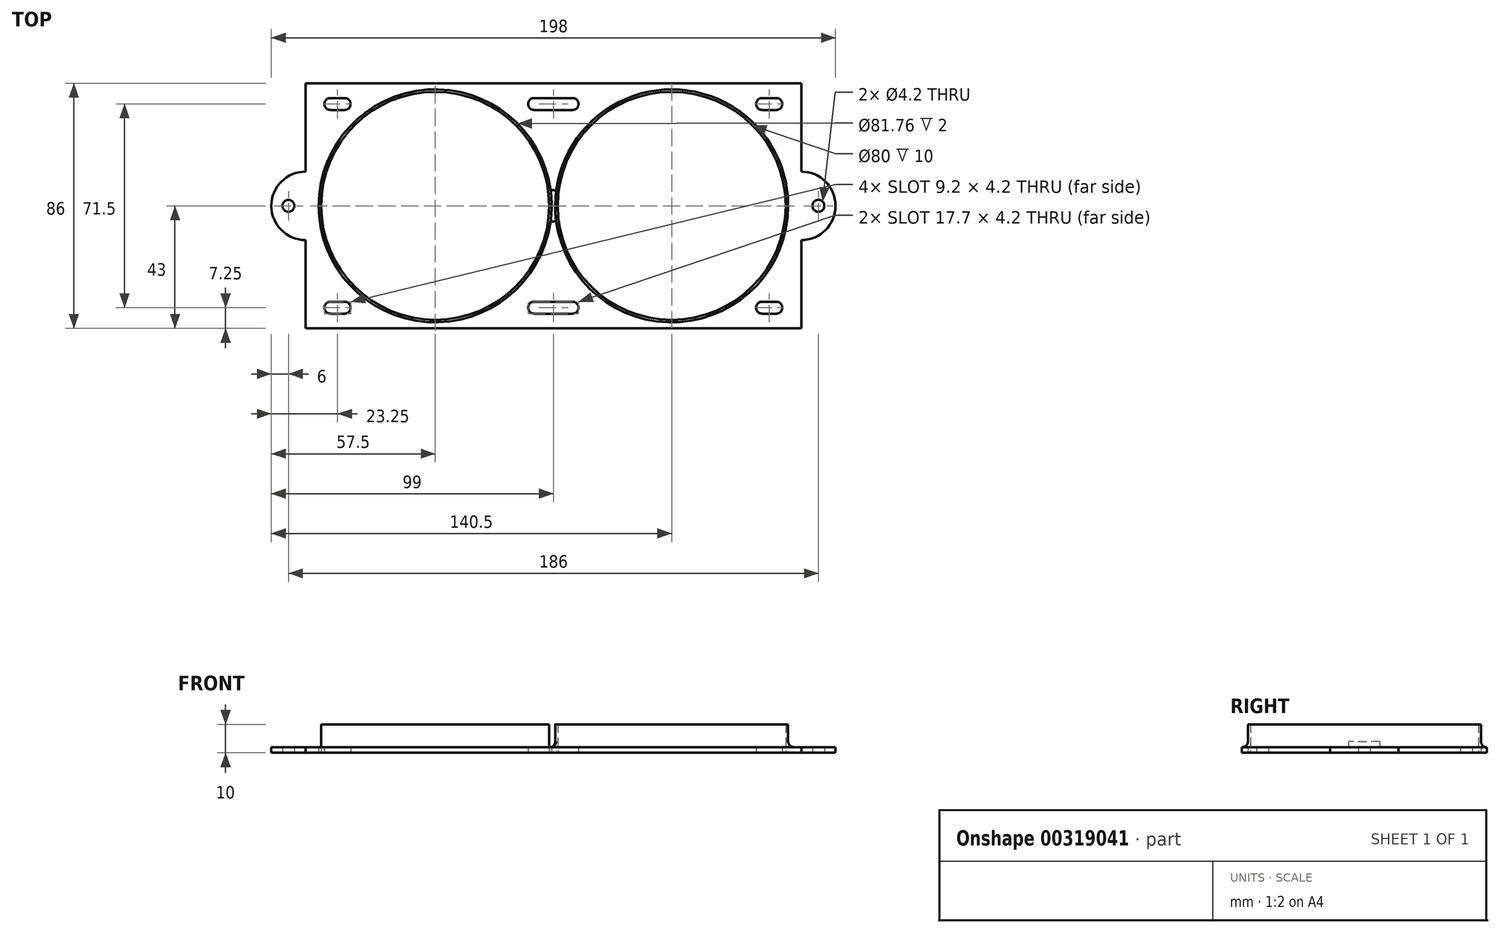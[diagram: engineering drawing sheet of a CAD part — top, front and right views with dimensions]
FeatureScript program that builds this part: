
annotation { "Feature Type Name" : "Feature", "Feature Type Description" : "" }
export const myFeature = defineFeature(function(context is Context, id is Id, definition is map)
    precondition{}
    {
        {
            var Q0;
            Q0=qCreatedBy(makeId("Top.planeOp"),FACE);
            var sketch = newSketch(context, id + "F0", { "sketchPlane" : qUnion([Q0])});
            skCircle(sketch, "E0", {"center": v(0, 0) * mm, "radius": 40 * mm});
            skLineSegment(sketch, "E1.bottom", {"start": v(35.75, -35.75) * mm, "end": v(-35.75, -35.75) * mm, "construction": true});
            skLineSegment(sketch, "E1.top", {"start": v(35.75, 35.75) * mm, "end": v(-35.75, 35.75) * mm, "construction": true});
            skLineSegment(sketch, "E1.left", {"start": v(35.75, -35.75) * mm, "end": v(35.75, 35.75) * mm, "construction": true});
            skLineSegment(sketch, "E1.right", {"start": v(-35.75, -35.75) * mm, "end": v(-35.75, 35.75) * mm, "construction": true});
            skLineSegment(sketch, "E2.bottom", {"start": v(41.5, -43) * mm, "end": v(-41.5, -43) * mm});
            skLineSegment(sketch, "E2.top", {"start": v(41.5, 43) * mm, "end": v(-41.5, 43) * mm});
            skLineSegment(sketch, "E2.left", {"start": v(41.5, -43) * mm, "end": v(41.5, 43) * mm});
            skLineSegment(sketch, "E2.right", {"start": v(-41.5, -43) * mm, "end": v(-41.5, 43) * mm});
            skLineSegment(sketch, "E3.bottom", {"start": v(45.5, 43) * mm, "end": v(41.5, 43) * mm});
            skLineSegment(sketch, "E3.top", {"start": v(45.5, -43) * mm, "end": v(41.5, -43) * mm});
            skLineSegment(sketch, "E3.left", {"start": v(45.5, 43) * mm, "end": v(45.5, -43) * mm});
            skLineSegment(sketch, "E3.right", {"start": v(41.5, 43) * mm, "end": v(41.5, -43) * mm});
            skLineSegment(sketch, "E4", {"start": v(36.75, 35.75) * mm, "end": v(31.75, 35.75) * mm});
            skArc(sketch, "E5.0.startCap", {"start": v(36.75, 37.85) * mm, "mid": v(38.85, 35.75) * mm, "end": v(36.75, 33.65) * mm});
            skArc(sketch, "E5.0.endCap", {"start": v(31.75, 33.65) * mm, "mid": v(29.65, 35.75) * mm, "end": v(31.75, 37.85) * mm});
            skLineSegment(sketch, "E5.0.left", {"start": v(36.75, 33.65) * mm, "end": v(31.75, 33.65) * mm});
            skLineSegment(sketch, "E5.0.right", {"start": v(36.75, 37.85) * mm, "end": v(31.75, 37.85) * mm});
            skArc(sketch, "E6.MirrorCS", {"start": v(-119.75, 37.85) * mm, "mid": v(-121.85, 35.75) * mm, "end": v(-119.75, 33.65) * mm});
            skArc(sketch, "E7.MirrorCS", {"start": v(-114.75, 33.65) * mm, "mid": v(-112.65, 35.75) * mm, "end": v(-114.75, 37.85) * mm});
            skLineSegment(sketch, "E8.MirrorCS", {"start": v(-119.75, 37.85) * mm, "end": v(-114.75, 37.85) * mm});
            skLineSegment(sketch, "E9.MirrorCS", {"start": v(-119.75, 33.65) * mm, "end": v(-114.75, 33.65) * mm});
            skLineSegment(sketch, "E10.MirrorCS", {"start": v(-119.75, 35.75) * mm, "end": v(-114.75, 35.75) * mm});
            skLineSegment(sketch, "E11.MirrorCS", {"start": v(-124.5, -43) * mm, "end": v(-124.5, 43) * mm});
            skPoint(sketch, "E12.MirrorP", {"position": v(-83, 0) * mm});
            skLineSegment(sketch, "E13.MirrorCS", {"start": v(-118.75, -35.75) * mm, "end": v(-47.25, -35.75) * mm, "construction": true});
            skLineSegment(sketch, "E14.MirrorCS", {"start": v(-124.5, 43) * mm, "end": v(-124.5, -43) * mm});
            skLineSegment(sketch, "E15.MirrorCS", {"start": v(-124.5, 43) * mm, "end": v(-41.5, 43) * mm});
            skLineSegment(sketch, "E16.MirrorCS", {"start": v(-47.25, -35.75) * mm, "end": v(-47.25, 35.75) * mm, "construction": true});
            skLineSegment(sketch, "E17.MirrorCS", {"start": v(-118.75, 35.75) * mm, "end": v(-47.25, 35.75) * mm, "construction": true});
            skCircle(sketch, "E18.MirrorC", {"center": v(-83, 0) * mm, "radius": 40 * mm});
            skLineSegment(sketch, "E19.MirrorCS", {"start": v(-124.5, -43) * mm, "end": v(-41.5, -43) * mm});
            skLineSegment(sketch, "E20.MirrorCS", {"start": v(-118.75, -35.75) * mm, "end": v(-118.75, 35.75) * mm, "construction": true});
            skLineSegment(sketch, "E21", {"start": v(0, 0) * mm, "end": v(-83, 0) * mm, "construction": true});
            skLineSegment(sketch, "E22", {"start": v(-40, 0) * mm, "end": v(-43, 0) * mm, "construction": true});
            skLineSegment(sketch, "E23", {"start": v(-34.75, 35.75) * mm, "end": v(-48.25, 35.75) * mm, "construction": true});
            skArc(sketch, "E24.0.startCap", {"start": v(-34.75, 37.85) * mm, "mid": v(-32.65, 35.75) * mm, "end": v(-34.75, 33.65) * mm});
            skArc(sketch, "E24.0.endCap", {"start": v(-48.25, 33.65) * mm, "mid": v(-50.35, 35.75) * mm, "end": v(-48.25, 37.85) * mm});
            skLineSegment(sketch, "E24.0.left", {"start": v(-34.75, 33.65) * mm, "end": v(-48.25, 33.65) * mm});
            skLineSegment(sketch, "E24.0.right", {"start": v(-34.75, 37.85) * mm, "end": v(-48.25, 37.85) * mm});
            skArc(sketch, "E25.MirrorCS", {"start": v(-48.25, -33.65) * mm, "mid": v(-50.35, -35.75) * mm, "end": v(-48.25, -37.85) * mm});
            skLineSegment(sketch, "E26.MirrorCS", {"start": v(-34.75, -33.65) * mm, "end": v(-48.25, -33.65) * mm});
            skArc(sketch, "E27.MirrorCS", {"start": v(-34.75, -37.85) * mm, "mid": v(-32.65, -35.75) * mm, "end": v(-34.75, -33.65) * mm});
            skLineSegment(sketch, "E28.MirrorCS", {"start": v(-34.75, -35.75) * mm, "end": v(-48.25, -35.75) * mm, "construction": true});
            skLineSegment(sketch, "E29.MirrorCS", {"start": v(-34.75, -37.85) * mm, "end": v(-48.25, -37.85) * mm});
            skLineSegment(sketch, "E30.MirrorCS", {"start": v(36.75, -37.85) * mm, "end": v(31.75, -37.85) * mm});
            skLineSegment(sketch, "E31.MirrorCS", {"start": v(36.75, -33.65) * mm, "end": v(31.75, -33.65) * mm});
            skLineSegment(sketch, "E32.MirrorCS", {"start": v(36.75, -35.75) * mm, "end": v(31.75, -35.75) * mm});
            skArc(sketch, "E33.MirrorCS", {"start": v(36.75, -37.85) * mm, "mid": v(38.85, -35.75) * mm, "end": v(36.75, -33.65) * mm});
            skArc(sketch, "E34.MirrorCS", {"start": v(31.75, -33.65) * mm, "mid": v(29.65, -35.75) * mm, "end": v(31.75, -37.85) * mm});
            skArc(sketch, "E35.MirrorCS", {"start": v(-119.75, -37.85) * mm, "mid": v(-121.85, -35.75) * mm, "end": v(-119.75, -33.65) * mm});
            skArc(sketch, "E36.MirrorCS", {"start": v(-114.75, -33.65) * mm, "mid": v(-112.65, -35.75) * mm, "end": v(-114.75, -37.85) * mm});
            skLineSegment(sketch, "E37.MirrorCS", {"start": v(-119.75, -35.75) * mm, "end": v(-114.75, -35.75) * mm});
            skLineSegment(sketch, "E38.MirrorCS", {"start": v(-119.75, -37.85) * mm, "end": v(-114.75, -37.85) * mm});
            skLineSegment(sketch, "E39.MirrorCS", {"start": v(-119.75, -33.65) * mm, "end": v(-114.75, -33.65) * mm});
            skLineSegment(sketch, "E40.MirrorCS", {"start": v(-128.5, 43) * mm, "end": v(-124.5, 43) * mm});
            skLineSegment(sketch, "E41.MirrorCS", {"start": v(-128.5, -43) * mm, "end": v(-124.5, -43) * mm});
            skLineSegment(sketch, "E42.MirrorCS", {"start": v(-128.5, 43) * mm, "end": v(-128.5, -43) * mm});
            skCircle(sketch, "E43", {"center": v(0, 0) * mm, "radius": 40.88 * mm});
            skCircle(sketch, "E44.MirrorC", {"center": v(-83, 0) * mm, "radius": 40.88 * mm});
            skPoint(sketch, "E45.center.orphan", {"position": v(45.5, 0) * mm});
            skArc(sketch, "E46.trimOffspring", {"start": v(45.5, -12) * mm, "mid": v(57.5, 0) * mm, "end": v(45.5, 12) * mm});
            skCircle(sketch, "E47", {"center": v(51.5, 0) * mm, "radius": 2.1 * mm});
            skLineSegment(sketch, "E48", {"start": v(57.5, 0) * mm, "end": v(45.5, 0) * mm, "construction": true});
            skPoint(sketch, "E49.MirrorP", {"position": v(-128.5, 0) * mm});
            skCircle(sketch, "E50.MirrorC", {"center": v(-134.5, 0) * mm, "radius": 2.1 * mm});
            skArc(sketch, "E51.MirrorCS", {"start": v(-128.5, -12) * mm, "mid": v(-140.5, 0) * mm, "end": v(-128.5, 12) * mm});
            skLineSegment(sketch, "E52.MirrorCS", {"start": v(-140.5, 0) * mm, "end": v(-128.5, 0) * mm, "construction": true});
            skSolve(sketch);
        }
        {
            var Q0;
            Q0 = qSketchRegion(id + "F0", true);
            var Q1;
            Q1=makeQuery(id+"F0.imprint","IMPRINT",FACE,{"disambiguationData":[TD([[makeQuery(id+"F0.imprint","IMPRINT",EDGE,{"derivedFrom":sQuery(id+"F0.wireOp",EDGE,"E0")}),-1.0]])]});
            var Q2;
            Q2=makeQuery(id+"F0.imprint","IMPRINT",FACE,{"disambiguationData":[TD([[makeQuery(id+"F0.imprint","IMPRINT",EDGE,{"derivedFrom":sQuery(id+"F0.wireOp",EDGE,"E18.MirrorC")}),1.0]])]});
            extrude(context, id + "F1", {"entities" : qUnion([Q0, Q1, Q2]), "depth" : 2 * mm});
        }
        {
            var Q0;
            Q0=makeQuery(id+"F0.imprint","IMPRINT",FACE,{"disambiguationData":[TD([[makeQuery(id+"F0.imprint","IMPRINT",EDGE,{"derivedFrom":sQuery(id+"F0.wireOp",EDGE,"E0")}),-1.0]])]});
            var Q1;
            Q1=makeQuery(id+"F0.imprint","IMPRINT",FACE,{"disambiguationData":[TD([[makeQuery(id+"F0.imprint","IMPRINT",EDGE,{"derivedFrom":sQuery(id+"F0.wireOp",EDGE,"E18.MirrorC")}),1.0]])]});
            extrude(context, id + "F2", {"entities" : qUnion([Q0, Q1]), "operationType" : NewBodyOperationType.ADD, "depth" : 10 * mm});
        }
        {
            var Q0;
            Q0=makeQuery(id+"F2.boolean.opBoolean","INTERSECT",EDGE,{"derivedFrom":[makeQuery(id+"F1.opExtrude","CAP_FACE",FACE,{"disambiguationData":[OSD([sQuery(id+"F0.wireOp",EDGE,"E0"),sQuery(id+"F0.wireOp",EDGE,"E2.bottom"),sQuery(id+"F0.wireOp",EDGE,"E2.top"),sQuery(id+"F0.wireOp",EDGE,"E3.bottom"),sQuery(id+"F0.wireOp",EDGE,"E3.top"),sQuery(id+"F0.wireOp",EDGE,"E3.left"),sQuery(id+"F0.wireOp",EDGE,"E5.0.startCap"),sQuery(id+"F0.wireOp",EDGE,"E5.0.endCap"),sQuery(id+"F0.wireOp",EDGE,"E5.0.left"),sQuery(id+"F0.wireOp",EDGE,"E5.0.right"),sQuery(id+"F0.wireOp",EDGE,"E15.MirrorCS"),sQuery(id+"F0.wireOp",EDGE,"E18.MirrorC"),sQuery(id+"F0.wireOp",EDGE,"E19.MirrorCS"),sQuery(id+"F0.wireOp",EDGE,"E24.0.startCap"),sQuery(id+"F0.wireOp",EDGE,"E24.0.endCap"),sQuery(id+"F0.wireOp",EDGE,"E24.0.left"),sQuery(id+"F0.wireOp",EDGE,"E24.0.right"),sQuery(id+"F0.wireOp",EDGE,"E25.MirrorCS"),sQuery(id+"F0.wireOp",EDGE,"E26.MirrorCS"),sQuery(id+"F0.wireOp",EDGE,"E27.MirrorCS"),sQuery(id+"F0.wireOp",EDGE,"E29.MirrorCS"),sQuery(id+"F0.wireOp",EDGE,"E30.MirrorCS"),sQuery(id+"F0.wireOp",EDGE,"E31.MirrorCS"),sQuery(id+"F0.wireOp",EDGE,"E33.MirrorCS"),sQuery(id+"F0.wireOp",EDGE,"E34.MirrorCS"),sQuery(id+"F0.wireOp",EDGE,"E40.MirrorCS"),sQuery(id+"F0.wireOp",EDGE,"E6.MirrorCS"),sQuery(id+"F0.wireOp",EDGE,"E38.MirrorCS"),sQuery(id+"F0.wireOp",EDGE,"E39.MirrorCS"),sQuery(id+"F0.wireOp",EDGE,"E8.MirrorCS"),sQuery(id+"F0.wireOp",EDGE,"E36.MirrorCS"),sQuery(id+"F0.wireOp",EDGE,"E9.MirrorCS"),sQuery(id+"F0.wireOp",EDGE,"E41.MirrorCS"),sQuery(id+"F0.wireOp",EDGE,"E7.MirrorCS"),sQuery(id+"F0.wireOp",EDGE,"E35.MirrorCS"),sQuery(id+"F0.wireOp",EDGE,"E42.MirrorCS"),sQuery(id+"F0.wireOp",EDGE,"E46.trimOffspring"),sQuery(id+"F0.wireOp",EDGE,"E47"),sQuery(id+"F0.wireOp",EDGE,"E50.MirrorC"),sQuery(id+"F0.wireOp",EDGE,"E51.MirrorCS")])],"isStart":false}),makeQuery(id+"F2.opExtrude","SWEPT_FACE",FACE,{"disambiguationData":[OSD([sQuery(id+"F0.wireOp",EDGE,"E44.MirrorC")])]})]});
            var Q1;
            Q1=makeQuery(id+"F2.boolean.opBoolean","INTERSECT",EDGE,{"derivedFrom":[makeQuery(id+"F1.opExtrude","CAP_FACE",FACE,{"disambiguationData":[OSD([sQuery(id+"F0.wireOp",EDGE,"E0"),sQuery(id+"F0.wireOp",EDGE,"E2.bottom"),sQuery(id+"F0.wireOp",EDGE,"E2.top"),sQuery(id+"F0.wireOp",EDGE,"E3.bottom"),sQuery(id+"F0.wireOp",EDGE,"E3.top"),sQuery(id+"F0.wireOp",EDGE,"E3.left"),sQuery(id+"F0.wireOp",EDGE,"E5.0.startCap"),sQuery(id+"F0.wireOp",EDGE,"E5.0.endCap"),sQuery(id+"F0.wireOp",EDGE,"E5.0.left"),sQuery(id+"F0.wireOp",EDGE,"E5.0.right"),sQuery(id+"F0.wireOp",EDGE,"E15.MirrorCS"),sQuery(id+"F0.wireOp",EDGE,"E18.MirrorC"),sQuery(id+"F0.wireOp",EDGE,"E19.MirrorCS"),sQuery(id+"F0.wireOp",EDGE,"E24.0.startCap"),sQuery(id+"F0.wireOp",EDGE,"E24.0.endCap"),sQuery(id+"F0.wireOp",EDGE,"E24.0.left"),sQuery(id+"F0.wireOp",EDGE,"E24.0.right"),sQuery(id+"F0.wireOp",EDGE,"E25.MirrorCS"),sQuery(id+"F0.wireOp",EDGE,"E26.MirrorCS"),sQuery(id+"F0.wireOp",EDGE,"E27.MirrorCS"),sQuery(id+"F0.wireOp",EDGE,"E29.MirrorCS"),sQuery(id+"F0.wireOp",EDGE,"E30.MirrorCS"),sQuery(id+"F0.wireOp",EDGE,"E31.MirrorCS"),sQuery(id+"F0.wireOp",EDGE,"E33.MirrorCS"),sQuery(id+"F0.wireOp",EDGE,"E34.MirrorCS"),sQuery(id+"F0.wireOp",EDGE,"E40.MirrorCS"),sQuery(id+"F0.wireOp",EDGE,"E6.MirrorCS"),sQuery(id+"F0.wireOp",EDGE,"E38.MirrorCS"),sQuery(id+"F0.wireOp",EDGE,"E39.MirrorCS"),sQuery(id+"F0.wireOp",EDGE,"E8.MirrorCS"),sQuery(id+"F0.wireOp",EDGE,"E36.MirrorCS"),sQuery(id+"F0.wireOp",EDGE,"E9.MirrorCS"),sQuery(id+"F0.wireOp",EDGE,"E41.MirrorCS"),sQuery(id+"F0.wireOp",EDGE,"E7.MirrorCS"),sQuery(id+"F0.wireOp",EDGE,"E35.MirrorCS"),sQuery(id+"F0.wireOp",EDGE,"E42.MirrorCS"),sQuery(id+"F0.wireOp",EDGE,"E46.trimOffspring"),sQuery(id+"F0.wireOp",EDGE,"E47"),sQuery(id+"F0.wireOp",EDGE,"E50.MirrorC"),sQuery(id+"F0.wireOp",EDGE,"E51.MirrorCS")])],"isStart":false}),makeQuery(id+"F2.opExtrude","SWEPT_FACE",FACE,{"disambiguationData":[OSD([sQuery(id+"F0.wireOp",EDGE,"E43")])]})]});
            fillet(context, id + "F3", {"entities" : qUnion([Q0, Q1]), "radius" : 2 * mm, "tangentPropagation" : true, "allowEdgeOverflow" : false});
        }
    });
